# Revit family: PRD_AR_FlshCntrlDvcs_F5-SmartUrinalUnit_ACEF3004 2
name_source: partatom
category: Specialty Equipment
units: mm (PartAtom-declared; Revit-internal decimal feet)

## family parameters
Always vertical = Yes
Cut with Voids When Loaded = No
Enable Cutting in Views = No
Maintain Annotation Orientation = No
OmniClass Number = 23.45.55.11
OmniClass Title = Sanitary Components
Part Type = Normal
Room Calculation Point = No
Round Connector Dimension = Use Diameter
Shared = No
Work Plane-Based = No

## types (1)
- ACEF3004
    AssetType = Fixed
    BIMObjectName = PRD_AR_FlushControlDevices_F5-SmartUrinalUnit_ACEF3004
    BodyMaterial = PRD_AR_Brass
    Category = Pr_75_50_46_31, Flush control devices
    CloseOffRating = 0.0 Pa
    Default Elevation = 0 mm  [stored 0 ft]
    Description = F5 smart urinal unit for installation within the water inlet area of the CAMPUS urinal series. Water path pre-assembled with pipe elbows for DN 15 water connection and flushing pipe, valve assembly with water volume regulation including a strainer, solenoid valve and hose. Control unit in sealed plastic box for wireless communication with the F5 smart urinal sensor. Either for battery operation with 6 V lithium battery (CR-P2) per control unit or separate power supply via power supply unit 6.75 V/12 V DC. Battery compartment including battery or power supply unit with extension cable must be ordered separately.
    Export Type to IFC As = IfcValveType
    Features = With pipe elbows for DN 15 water connection and flushing pipe.
    FlowCoefficient = 0
    FlushingRate = 0.0 L/s
    HasIntegralShutOffDevice = Yes
    IfcExportAs = IfcValve
    IfcExportType = FLUSHING
    IsHighPressure = No
    Manufacturer = KWC Group Management AG
    ManufacturerName = KWC Group Management AG
    ManufacturerURL = www.kwc-professional.com
    Model = ACEF3004
    ModelNumber = 2030072412
    ModelReference = ACEF3004
    NBSDescription = Flush control devices
    NBSReference = 90-15-35/470
    Name = Smart urinal unit for series of urinals made of stainless steel ACEF3004
    NominalDepth = 0 mm  [stored 0 ft]
    NominalHeight = 0 mm  [stored 0 ft]
    NominalWidth = 0 mm  [stored 0 ft]
    ProductInformation = http://pim.kwc.com
    Quantity = 1
    QuantityUOM = piece
    QuaternaryMaterial = PRD_AR_Plastic_White
    SecondaryMaterial = PRD_AR_Plastic_Black
    Size = 15 mm  [stored 0.0492126 ft]
    Status = New
    TertiaryMaterial = PRD_AR_StainlessSteel_SatinFinished
    TestPressure = 0.0 Pa
    Type IFC Predefined Type = FLUSHING
    URL = www.kwc-professional.com
    Uniclass2015Code = Pr_75_50_46_31
    Uniclass2015Title = Flush control devices
    Uniclass2015Version = Products v1.38
    ValveMechanism = OTHER
    ValveOperation = SOLENOID
    ValvePattern = STRAIGHT_2_PORT
    Version = 1
    WorkingPressure = 0.0 Pa

note: [stored X ft] marks values corroborated as IEEE doubles in the binary element streams (Revit-internal decimal feet)

## geometry (parser evidence)
native form markers: Sweep x2
no freeform markers — native parametric forms only
